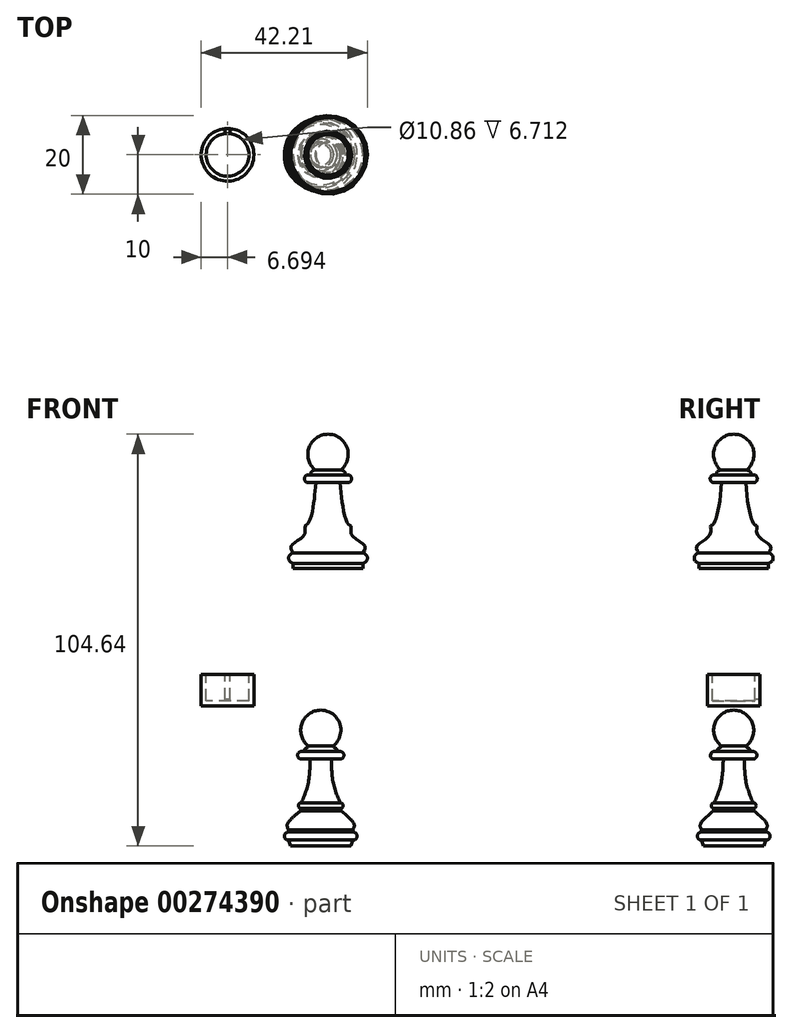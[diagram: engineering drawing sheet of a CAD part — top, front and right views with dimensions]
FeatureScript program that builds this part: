
annotation { "Feature Type Name" : "Feature", "Feature Type Description" : "" }
export const myFeature = defineFeature(function(context is Context, id is Id, definition is map)
    precondition{}
    {
        {
            var Q0;
            Q0=qCreatedBy(makeId("Front.planeOp"),FACE);
            var sketch = newSketch(context, id + "F0", { "sketchPlane" : qUnion([Q0])});
            skLineSegment(sketch, "E0", {"start": v(1.87, -63) * mm, "end": v(27.27, -63) * mm});
            skLineSegment(sketch, "E1", {"start": v(145.5, -38.95) * mm, "end": v(145.5, -28.3) * mm, "construction": true});
            skArc(sketch, "E2", {"start": v(148.78, -38.95) * mm, "mid": v(150.33, -33.26) * mm, "end": v(145.5, -29.87) * mm});
            skFitSpline(sketch, "E3", {"points": [v(148.78, -38.95) * mm, v(149.69, -39.35) * mm, v(149.92, -40.18) * mm], "startDerivative": vector(2.09, -0.52) * mm, "endDerivative": vector(0.18, -1.96) * mm});
            skLineSegment(sketch, "E4", {"start": v(149.92, -40.18) * mm, "end": v(150.82, -40.18) * mm});
            skArc(sketch, "E5", {"start": v(150.82, -42.17) * mm, "mid": v(151.49, -41.18) * mm, "end": v(150.82, -40.18) * mm});
            skLineSegment(sketch, "E6", {"start": v(150.82, -42.17) * mm, "end": v(148.6, -42.17) * mm});
            skFitSpline(sketch, "E7", {"points": [v(148.6, -42.17) * mm, v(149.5, -49.48) * mm, v(150.87, -52.91) * mm, v(151.35, -53.22) * mm, v(151.5, -55.37) * mm, v(154.86, -58.27) * mm, v(154.34, -60.02) * mm], "startDerivative": vector(2.36, -28.85) * mm, "endDerivative": vector(-9.52, -13.55) * mm});
            skArc(sketch, "E8", {"start": v(154.34, -62.65) * mm, "mid": v(155.5, -61.33) * mm, "end": v(154.34, -60.02) * mm});
            skLineSegment(sketch, "E9", {"start": v(154.34, -62.65) * mm, "end": v(154.34, -64.01) * mm});
            skLineSegment(sketch, "E10", {"start": v(154.34, -64.01) * mm, "end": v(145.5, -64.01) * mm});
            skLineSegment(sketch, "E11", {"start": v(145.5, -29.87) * mm, "end": v(145.5, -64.01) * mm});
            skPoint(sketch, "E11.endSnap0", {"position": v(145.5, -33.62) * mm});
            skArc(sketch, "E12", {"start": v(146.9, -109.03) * mm, "mid": v(148.47, -103.36) * mm, "end": v(143.67, -99.97) * mm});
            skLineSegment(sketch, "E13", {"start": v(143.67, -109.03) * mm, "end": v(143.67, -99.97) * mm});
            skLineSegment(sketch, "E14", {"start": v(143.67, -109.03) * mm, "end": v(143.67, -134.51) * mm});
            skFitSpline(sketch, "E15", {"points": [v(146.9, -109.03) * mm, v(146.9, -109.4) * mm, v(147.59, -109.7) * mm, v(147.76, -110.48) * mm], "startDerivative": vector(-0.5, -1.64) * mm, "endDerivative": vector(-0.07, -2.43) * mm});
            skLineSegment(sketch, "E16", {"start": v(147.76, -110.48) * mm, "end": v(148.6, -110.48) * mm});
            skLineSegment(sketch, "E17", {"start": v(148.6, -112.4) * mm, "end": v(146.32, -112.4) * mm});
            skArc(sketch, "E18", {"start": v(148.6, -112.4) * mm, "mid": v(149.56, -111.44) * mm, "end": v(148.6, -110.48) * mm});
            skFitSpline(sketch, "E19", {"points": [v(146.32, -112.4) * mm, v(146.9, -118.67) * mm, v(148.62, -123.54) * mm], "startDerivative": vector(0.45, -12.38) * mm, "endDerivative": vector(4.21, -9.83) * mm});
            skArc(sketch, "E20", {"start": v(148.86, -124.91) * mm, "mid": v(149.36, -124.11) * mm, "end": v(148.62, -123.54) * mm});
            skLineSegment(sketch, "E21", {"start": v(148.86, -124.91) * mm, "end": v(148.86, -125.6) * mm});
            skFitSpline(sketch, "E22", {"points": [v(148.86, -125.6) * mm, v(152.17, -129.07) * mm, v(151.8, -130.35) * mm], "startDerivative": vector(7.05, -5.83) * mm, "endDerivative": vector(-2.1, -3.45) * mm});
            skLineSegment(sketch, "E23", {"start": v(151.8, -130.35) * mm, "end": v(151.8, -130.96) * mm});
            skArc(sketch, "E24", {"start": v(151.8, -132.99) * mm, "mid": v(152.92, -131.97) * mm, "end": v(151.8, -130.96) * mm});
            skLineSegment(sketch, "E25", {"start": v(151.8, -132.99) * mm, "end": v(151.33, -134.51) * mm});
            skLineSegment(sketch, "E26", {"start": v(151.33, -134.51) * mm, "end": v(143.67, -134.51) * mm});
            skPoint(sketch, "E27.orphan", {"position": v(140.43, -109.03) * mm});
            skLineSegment(sketch, "E28.bottom", {"start": v(119.98, -90.91) * mm, "end": v(126.68, -90.91) * mm});
            skLineSegment(sketch, "E28.top", {"start": v(119.98, -98.9) * mm, "end": v(126.68, -98.9) * mm});
            skLineSegment(sketch, "E28.right", {"start": v(126.68, -90.91) * mm, "end": v(126.68, -98.9) * mm});
            skLineSegment(sketch, "E29", {"start": v(119.98, -90.91) * mm, "end": v(119.98, -98.9) * mm});
            skSolve(sketch);
        }
        {
            var Q0;
            Q0=makeQuery(id+"F0.imprint","IMPRINT",FACE,{"disambiguationData":[TD([[makeQuery(id+"F0.imprint","IMPRINT",EDGE,{"derivedFrom":sQuery(id+"F0.wireOp",EDGE,"E2")}),1.0]])]});
            var Q1;
            Q1=sQuery(id+"F0.wireOp",EDGE,"E11");
            revolve(context, id + "F1", {"entities" : qUnion([Q0]), "axis" : qUnion([Q1]), "revolveType" : RevolveType.FULL});
        }
        {
            var Q0;
            Q0=makeQuery(id+"F0.imprint","IMPRINT",FACE,{"disambiguationData":[TD([[makeQuery(id+"F0.imprint","IMPRINT",EDGE,{"derivedFrom":sQuery(id+"F0.wireOp",EDGE,"E12")}),1.0]])]});
            var Q1;
            Q1=sQuery(id+"F0.wireOp",EDGE,"E14");
            revolve(context, id + "F2", {"entities" : qUnion([Q0]), "axis" : qUnion([Q1]), "revolveType" : RevolveType.FULL});
        }
        {
            var Q0;
            Q0=makeQuery(id+"F0.imprint","IMPRINT",FACE,{"disambiguationData":[TD([[makeQuery(id+"F0.imprint","IMPRINT",EDGE,{"derivedFrom":sQuery(id+"F0.wireOp",EDGE,"E28.bottom")}),-1.0]])]});
            var Q1;
            Q1=sQuery(id+"F0.wireOp",EDGE,"E29");
            revolve(context, id + "F3", {"entities" : qUnion([Q0]), "axis" : qUnion([Q1]), "revolveType" : RevolveType.FULL});
        }
        {
            var Q0;
            Q0=makeQuery(id+"F3.opRevolve","SWEPT_FACE",FACE,{"disambiguationData":[OSD([sQuery(id+"F0.wireOp",EDGE,"E28.bottom")])]});
            shell(context, id + "F4", {"entities" : qUnion([Q0]), "thickness" : 1.27 * mm});
        }
        {
            var Q0;
            Q0=makeQuery(id+"F3.opRevolve","SWEPT_FACE",FACE,{"disambiguationData":[OSD([sQuery(id+"F0.wireOp",EDGE,"E28.bottom")])]});
            var sketch = newSketch(context, id + "F5", { "sketchPlane" : qUnion([Q0])});
            skLineSegment(sketch, "E30", {"start": v(119.98, 0) * mm, "end": v(119.98, 9.14) * mm, "construction": true});
            skLineSegment(sketch, "E31.bottom", {"start": v(120.6, 7.52) * mm, "end": v(119.37, 7.52) * mm});
            skLineSegment(sketch, "E31.left", {"start": v(120.6, 7.52) * mm, "end": v(120.6, 4.85) * mm});
            skLineSegment(sketch, "E31.right", {"start": v(119.37, 7.52) * mm, "end": v(119.37, 4.85) * mm});
            skPoint(sketch, "E31.middle", {"position": v(119.98, 0) * mm});
            skLineSegment(sketch, "E32", {"start": v(120.6, 4.85) * mm, "end": v(119.37, 4.85) * mm});
            skPoint(sketch, "E31.top.end.orphan", {"position": v(119.37, -7.52) * mm});
            skPoint(sketch, "E31.top.start.orphan", {"position": v(120.6, -7.52) * mm});
            skSolve(sketch);
        }
        {
            var Q0;
            {var subQ0=sQuery(id+"F5.wireOp",EDGE,"E31.left");var subQ1=sQuery(id+"F0.wireOp",EDGE,"E28.right");var subQ2=sQuery(id+"F0.wireOp",EDGE,"E28.bottom");var subQ3=makeQuery(id+"F3.opRevolve","SWEPT_EDGE",EDGE,{"disambiguationData":[OSD([subQ2,subQ1])]});var subQ4=makeQuery(id+"F5.imprint","INTERSECT",VERTEX,{"derivedFrom":[subQ3,subQ0]});Q0=makeQuery(id+"F5.imprint","IMPRINT",FACE,{"disambiguationData":[TD([[makeQuery(id+"F5.imprint","IMPRINT",EDGE,{"disambiguationData":[TD([[subQ4,-1.0]])],"derivedFrom":subQ0}),-1.0]])]});}
            extrude(context, id + "F6", {"entities" : qUnion([Q0]), "operationType" : NewBodyOperationType.REMOVE, "oppositeDirection" : true, "depth" : 6.35 * mm});
        }
    });
